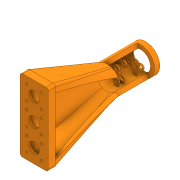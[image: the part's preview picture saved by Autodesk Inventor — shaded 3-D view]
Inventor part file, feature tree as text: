
AUTODESK INVENTOR PART (.ipt)
format: ipt  version: 2020 (Build 240168000, 168)  size: 669,184 bytes
history: native  units: in
note: dims shown in document units (in); Inventor stores cm internally (conversion verified against a paired STEP export)
features: sketch x18, extrude x15, projected_geometry x9, plane x3, loft x2, chamfer x1, other x1
ambient origin geometry x8: Origin, YZ Plane, XZ Plane, XY Plane, X Axis, Y Axis, Z Axis, Center Point
bodies: Solid1 (feature_tree)
feature tree (49):
  extrude  "Extrusion1"  Depth=2.0472in
  extrude  "Extrusion2"  Depth=1.6535in
  chamfer  "Chamfer1"  Distance=0.5512in
  extrude  "Extrusion3"  Depth=0.0157in
  extrude  "Extrusion4"  Depth=0.2756in TaperAngle=0.0deg
  extrude  "Extrusion5"  Depth=0.315in
  extrude  "Extrusion6"  Depth=0.4724in
  extrude  "Extrusion7"  Depth=0.0787in
  plane  "Work Plane1"
  extrude  "Extrusion8"  Depth=0.1575in
  plane  "Work Plane2"
  extrude  "Extrusion9"  Depth=1.0994in
  sketch  "Sketch11"  dims[d31=15.0deg d32=0.4921in d33=0.0in]
  plane  "Work Plane3"
  extrude  "Extrusion10"  Depth=0.4921in TaperAngle=0.0deg
  extrude  "Extrusion11"  Depth=1.5748in TaperAngle=360.0deg
  loft  "Loft1"
  loft  "Loft2"
  sketch  "Sketch16"  dims[d47=0.315in d48=0.4331in]
  extrude  "Extrusion12"  Depth=0.0787in TaperAngle=0.0deg
  extrude  "Extrusion13"  Depth=0.4331in
  extrude  "Extrusion14"  Depth=0.6161in
  extrude  "Extrusion15"  Depth=0.1575in
  sketch  "Sketch1"  dims[d0=2.3622in d1=2.0472in]
  sketch  "Sketch2"  dims[d2=0.2756in d3=0.0in d4=1.6535in d5=0.5512in d6=0.0in]
  sketch  "Sketch3"  dims[d7=0.2756in d8=0.125in d9=0.0137in d10=0.0157in]
  sketch  "Sketch5"  dims[d11=4.7244in d13=360.0deg d15=0.2756in d16=0.0in]
  sketch  "Sketch6"  dims[d17=0.5512in d19=0.315in]
  projected_geometry  "Projected Loop1"
  sketch  "Sketch7"  dims[d20=0.315in d21=0.4724in]
  projected_geometry  "Projected Loop2"
  sketch  "Sketch8"  dims[d22=0.4724in d23=0.0787in d24=0.0787in d25=0.0787in]
  projected_geometry  "Projected Loop3"
  sketch  "Sketch9"  dims[d26=0.0984in d27=0.0in d28=0.1575in]
  sketch  "Sketch10"  dims[d29=0.1575in d30=1.0994in]
  sketch  "Sketch12"  dims[d34=1.4567in d35=0.0in d36=1.5748in d38=360.0deg]
  sketch  "Sketch13"  dims[d40=0.0787in d41=0.0787in]
  projected_geometry  "Projected Loop4"
  other  "Edges1"
  sketch  "Sketch14"  dims[d42=0.0787in d43=0.0787in]
  projected_geometry  "Projected Loop5"
  sketch  "Sketch15"  dims[d44=0.0787in d45=0.0984in d46=0.0in]
  projected_geometry  "Projected Loop6"
  projected_geometry  "Projected Loop7"
  sketch  "Sketch19"  dims[d49=0.0984in d50=0.0in d51=0.6161in]
  projected_geometry  "Projected Loop8"
  sketch  "Sketch20"  dims[d52=0.1575in d53=0.1575in]
  projected_geometry  "Projected Loop9"
  sketch  "Sketch21"  dims[d54=0.0984in d55=0.0in d56=6.6929in d57=0.8858in d58=1.6654in d59=1.6654in d60=0.0in d61=0.0in d62=1.6654in d63=1.6654in d64=0.1969in d65=0.1969in d66=0.3484in d67=0.3484in d68=0.1969in d69=0.1969in d70=0.1969in d71=0.3937in d72=0.0in d73=0.7874in d74=0.0in d75=0.0in d76=90.0deg d77=0.0in d78=90.0deg d79=0.0in d80=90.0deg d81=0.0in d82=90.0deg d86=0.7874in d87=0.0in d90=0.3937in d91=0.3937in d92=0.7874in d93=0.0in d94=0.1969in d95=0.0in d96=0.8858in d97=1.6654in d98=1.6654in d99=0.0in d100=0.0in d101=0.2224in d102=0.1575in d103=0.1575in d104=0.1575in d105=0.1575in d106=0.0984in d107=0.0984in d108=0.1969in d109=0.0in]
